# Revit family: SLG - pannello  da 3_cotto smaltato
name_source: partatom
category: Curtain Panels
revit_build: Autodesk Revit 2014 (Build: 20130308_1515(x64)
units: mm (PartAtom-declared; Revit-internal decimal feet)

## types (21) — shared parameters
Analytic Construction = <None>

## per-type parameters (varying)
| type | cotto interno | cotto lab 2mb |
| 01 - Cotto | SLG - Cotto smaltato viola | SLG - Cotto |
| 02 - Arancio | SLG - Cotto smaltato arancio 303 | SLG - Cotto smaltato arancio 303 |
| 03 - Azzurro | SLG - Cotto smaltato azzurro | SLG - Cotto smaltato azzurro |
| 04 - Giallo | SLG - Cotto smaltato giallo 201 | SLG - Cotto smaltato giallo 201 |
| 05 - Lilla | SLG - Cotto smaltato lilla 809 | SLG - Cotto smaltato lilla 809 |
| 06 - Rosso | SLG - Cotto smaltato rosso 403 | SLG - Cotto smaltato rosso 403 |
| 07 - Verde ghiaccio | SLG - Cotto smaltato verde ghiaccio | SLG - Cotto smaltato verde ghiaccio |
| 08 - Verde acido | SLG - Cotto smaltato verde acido | SLG - Cotto smaltato verde acido |
| 09 - Verde petrolio | SLG - Cotto smaltato verde petrolio | SLG - Cotto smaltato verde petrolio |
| 10 - Viola | SLG - Cotto smaltato viola | SLG - Cotto smaltato viola |
| 11 - Verde smeraldo | SLG - Cotto smaltato verde smeraldo | SLG - Cotto smaltato verde smeraldo |
| 12 - cotto+arancio | SLG - Cotto smaltato arancio 303 | SLG - Cotto |
| 13 - cotto+azzurro | SLG - Cotto smaltato azzurro | SLG - Cotto |
| 14 - cotto+giallo | SLG - Cotto smaltato giallo 201 | SLG - Cotto |
| 15 - cotto+lilla | SLG - Cotto smaltato lilla 809 | SLG - Cotto |
| 16 - cotto+rosso | SLG - Cotto smaltato rosso 403 | SLG - Cotto |
| 17 - cotto+verde acido | SLG - Cotto smaltato verde acido | SLG - Cotto |
| 18 - cotto+verde ghiaccio | SLG - Cotto smaltato verde ghiaccio | SLG - Cotto |
| 19 - cotto+verde petrolio | SLG - Cotto smaltato verde petrolio | SLG - Cotto |
| 20 - cotto+verde smeraldo | SLG - Cotto smaltato verde smeraldo | SLG - Cotto |
| 21 - cotto+viola | SLG - Cotto smaltato viola | SLG - Cotto |

## geometry (parser evidence)
native form markers: Sweep x13
no freeform markers — native parametric forms only
